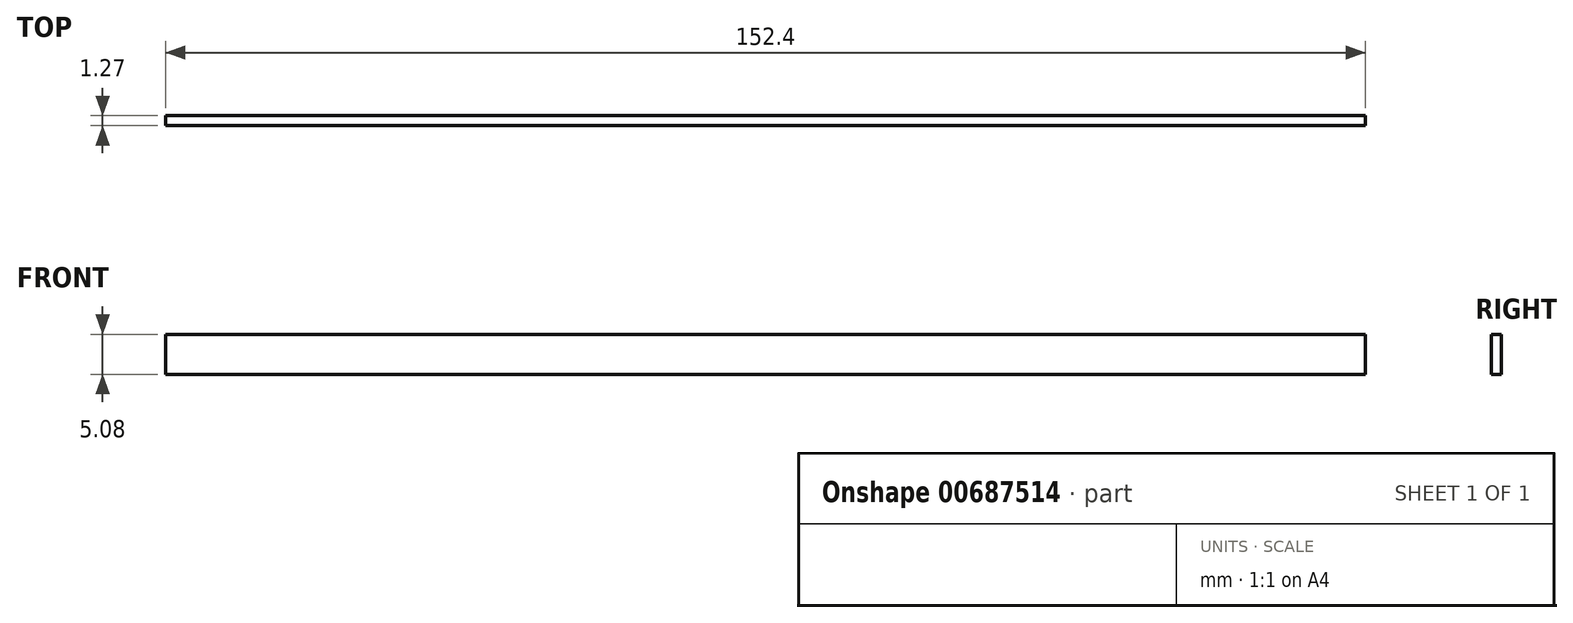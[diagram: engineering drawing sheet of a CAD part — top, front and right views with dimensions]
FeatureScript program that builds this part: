
annotation { "Feature Type Name" : "Feature", "Feature Type Description" : "" }
export const myFeature = defineFeature(function(context is Context, id is Id, definition is map)
    precondition{}
    {
        {
            var Q0;
            Q0=qCreatedBy(makeId("Front.planeOp"),FACE);
            var sketch = newSketch(context, id + "F0", { "sketchPlane" : qUnion([Q0])});
            skLineSegment(sketch, "E0.bottom", {"start": v(-25.66, 3.17) * mm, "end": v(126.74, 3.17) * mm});
            skLineSegment(sketch, "E0.top", {"start": v(-25.66, -1.9) * mm, "end": v(126.74, -1.9) * mm});
            skLineSegment(sketch, "E0.left", {"start": v(-25.66, 3.17) * mm, "end": v(-25.66, -1.9) * mm});
            skLineSegment(sketch, "E0.right", {"start": v(126.74, 3.17) * mm, "end": v(126.74, -1.9) * mm});
            skSolve(sketch);
        }
        {
            var Q0;
            Q0=qSketchRegion(id+"F0",true);
            extrude(context, id + "F1", {"entities" : qUnion([Q0]), "depth" : 1.27 * mm, "offsetDistance" : 25.4 * mm});
        }
    });
